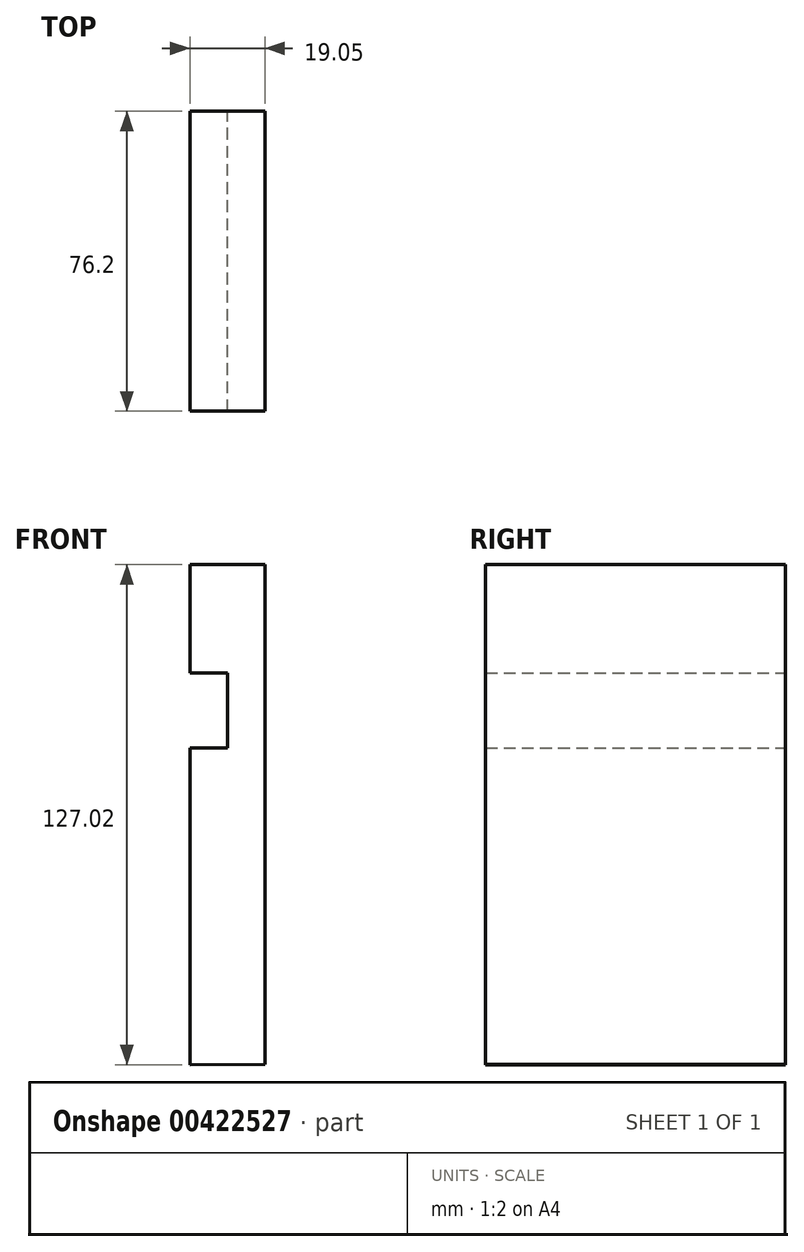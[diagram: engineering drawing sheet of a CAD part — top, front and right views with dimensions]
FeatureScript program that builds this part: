
annotation { "Feature Type Name" : "Feature", "Feature Type Description" : "" }
export const myFeature = defineFeature(function(context is Context, id is Id, definition is map)
    precondition{}
    {
        {
            var Q0;
            Q0=qCreatedBy(makeId("Front.planeOp"),FACE);
            var sketch = newSketch(context, id + "F0", { "sketchPlane" : qUnion([Q0])});
            skLineSegment(sketch, "E0", {"start": v(0, -73.35) * mm, "end": v(0, 53.65) * mm});
            skLineSegment(sketch, "E1", {"start": v(0, 53.65) * mm, "end": v(-19.05, 53.65) * mm});
            skLineSegment(sketch, "E2", {"start": v(-19.05, 53.65) * mm, "end": v(-19.05, 26.12) * mm});
            skLineSegment(sketch, "E3", {"start": v(-19.05, 26.12) * mm, "end": v(-9.52, 26.12) * mm});
            skLineSegment(sketch, "E4", {"start": v(-9.52, 26.12) * mm, "end": v(-9.52, 7.07) * mm});
            skLineSegment(sketch, "E5", {"start": v(-9.52, 7.07) * mm, "end": v(-19.05, 7.07) * mm});
            skLineSegment(sketch, "E6", {"start": v(-19.05, 7.07) * mm, "end": v(-19.05, -73.37) * mm});
            skLineSegment(sketch, "E7", {"start": v(0, -73.35) * mm, "end": v(-19.05, -73.37) * mm});
            skSolve(sketch);
        }
        {
            var Q0;
            Q0 = qSketchRegion(id + "F0", true);
            extrude(context, id + "F1", {"entities" : qUnion([Q0]), "depth" : 76.2 * mm});
        }
    });
